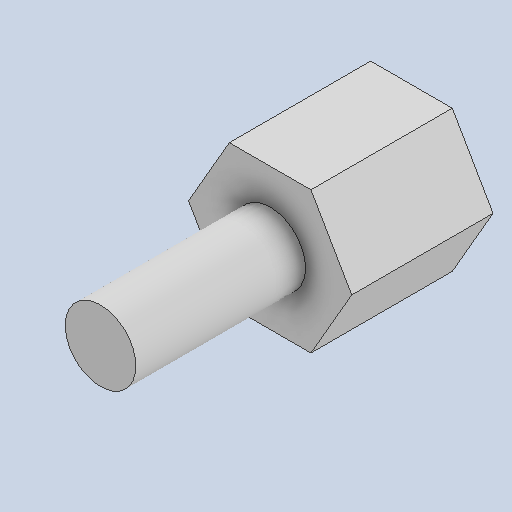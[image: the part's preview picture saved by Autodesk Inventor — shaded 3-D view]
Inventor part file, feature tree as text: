
AUTODESK INVENTOR PART (.ipt)
format: ipt  version: 2024.2 (Build 282272000, 272)  size: 118,784 bytes
history: native  units: mm
features: extrude x4, sketch x1, projected_geometry x1
ambient origin geometry x8: Origin, YZ Plane, XZ Plane, XY Plane, X Axis, Y Axis, Z Axis, Center Point
bodies: Solid1 (feature_tree)
feature tree (6):
  extrude  "Extrusion1"  Depth=5.0mm TaperAngle=0.0deg
  extrude  "Extrusion3"  Depth=3.0mm
  extrude  "Extrusion4"  Depth=3.0mm TaperAngle=0.0deg
  extrude  "Extrusion5"  Depth=3.0mm
  sketch  "Sketch1"  dims[d0=5.0mm d1=5.0mm d2=0.0mm d6=2.5mm d7=7.0mm d8=0.0mm d9=2.5mm d10=6.0mm d11=0.0mm d12=3.0mm d13=0.0mm]
  projected_geometry  "Projected Loop1"
